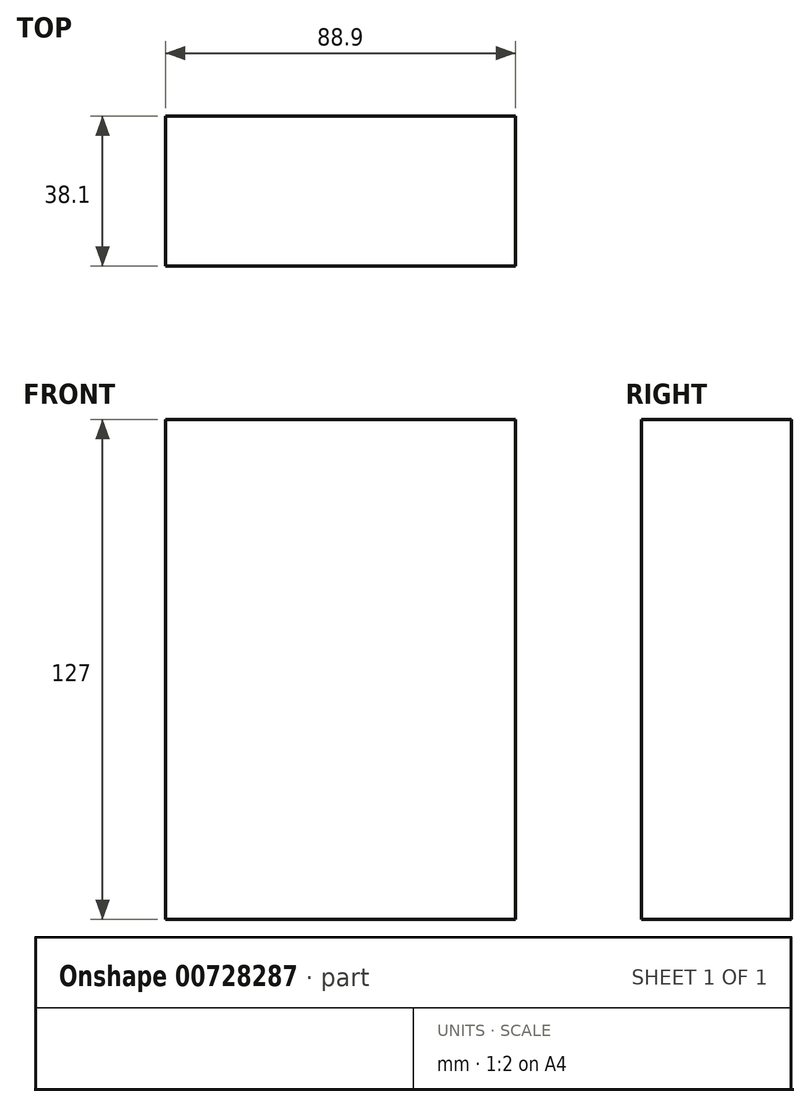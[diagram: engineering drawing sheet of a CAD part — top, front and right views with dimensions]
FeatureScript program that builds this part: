
annotation { "Feature Type Name" : "Feature", "Feature Type Description" : "" }
export const myFeature = defineFeature(function(context is Context, id is Id, definition is map)
    precondition{}
    {
        {
            var Q0;
            Q0=qCreatedBy(makeId("Front.planeOp"),FACE);
            var sketch = newSketch(context, id + "F0", { "sketchPlane" : qUnion([Q0])});
            skLineSegment(sketch, "E0.bottom", {"start": v(-44.45, -63.5) * mm, "end": v(44.45, -63.5) * mm});
            skLineSegment(sketch, "E0.top", {"start": v(-44.45, 63.5) * mm, "end": v(44.45, 63.5) * mm});
            skLineSegment(sketch, "E0.left", {"start": v(-44.45, -63.5) * mm, "end": v(-44.45, 63.5) * mm});
            skLineSegment(sketch, "E0.right", {"start": v(44.45, -63.5) * mm, "end": v(44.45, 63.5) * mm});
            skPoint(sketch, "E0.middle", {"position": v(0, 0) * mm});
            skSolve(sketch);
        }
        {
            var Q0;
            Q0=qSketchRegion(id+"F0",true);
            extrude(context, id + "F1", {"entities" : qUnion([Q0]), "depth" : 38.1 * mm, "offsetDistance" : 25.4 * mm});
        }
    });
